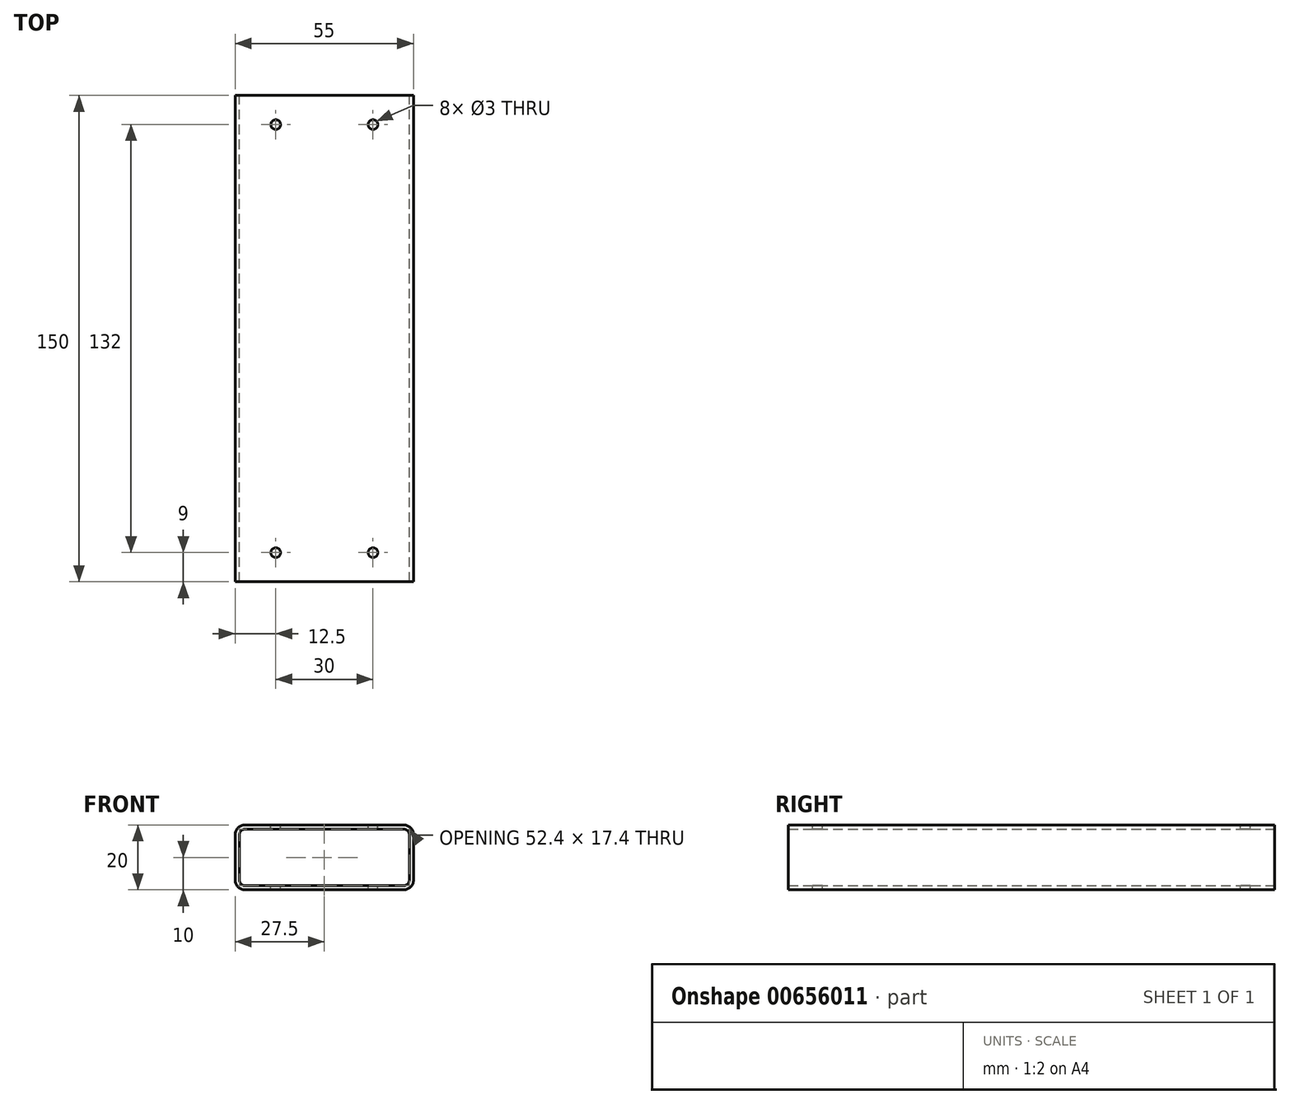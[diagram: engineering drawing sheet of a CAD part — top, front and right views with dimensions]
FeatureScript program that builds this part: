
annotation { "Feature Type Name" : "Feature", "Feature Type Description" : "" }
export const myFeature = defineFeature(function(context is Context, id is Id, definition is map)
    precondition{}
    {
        {
            var Q0;
            Q0=qCreatedBy(makeId("Front.planeOp"),FACE);
            var sketch = newSketch(context, id + "F0", { "sketchPlane" : qUnion([Q0])});
            skLineSegment(sketch, "E0.bottom", {"start": v(-24.5, 10) * mm, "end": v(24.5, 10) * mm});
            skLineSegment(sketch, "E0.top", {"start": v(-24.5, -10) * mm, "end": v(24.5, -10) * mm});
            skLineSegment(sketch, "E0.left", {"start": v(-27.5, 7) * mm, "end": v(-27.5, -7) * mm});
            skLineSegment(sketch, "E0.right", {"start": v(27.5, 7) * mm, "end": v(27.5, -7) * mm});
            skPoint(sketch, "E0.middle", {"position": v(0, 0) * mm});
            skLineSegment(sketch, "E1.bottom", {"start": v(-24.5, 8.7) * mm, "end": v(24.5, 8.7) * mm});
            skLineSegment(sketch, "E1.top", {"start": v(-24.5, -8.7) * mm, "end": v(24.5, -8.7) * mm});
            skLineSegment(sketch, "E1.left", {"start": v(-26.2, 7) * mm, "end": v(-26.2, -7) * mm});
            skLineSegment(sketch, "E1.right", {"start": v(26.2, 7) * mm, "end": v(26.2, -7) * mm});
            skPoint(sketch, "E2.visualSharp", {"position": v(-26.2, 8.7) * mm});
            skArc(sketch, "E2.filletArc", {"start": v(-24.5, 8.7) * mm, "mid": v(-25.7, 8.2) * mm, "end": v(-26.2, 7) * mm});
            skPoint(sketch, "E3.visualSharp", {"position": v(26.2, 8.7) * mm});
            skArc(sketch, "E3.filletArc", {"start": v(26.2, 7) * mm, "mid": v(25.7, 8.2) * mm, "end": v(24.5, 8.7) * mm});
            skPoint(sketch, "E4.visualSharp", {"position": v(26.2, -8.7) * mm});
            skArc(sketch, "E4.filletArc", {"start": v(24.5, -8.7) * mm, "mid": v(25.7, -8.2) * mm, "end": v(26.2, -7) * mm});
            skPoint(sketch, "E5.visualSharp", {"position": v(-26.2, -8.7) * mm});
            skArc(sketch, "E5.filletArc", {"start": v(-26.2, -7) * mm, "mid": v(-25.7, -8.2) * mm, "end": v(-24.5, -8.7) * mm});
            skPoint(sketch, "E6.visualSharp", {"position": v(-27.5, 10) * mm});
            skArc(sketch, "E6.filletArc", {"start": v(-24.5, 10) * mm, "mid": v(-26.62, 9.12) * mm, "end": v(-27.5, 7) * mm});
            skPoint(sketch, "E7.visualSharp", {"position": v(27.5, 10) * mm});
            skArc(sketch, "E7.filletArc", {"start": v(27.5, 7) * mm, "mid": v(26.62, 9.12) * mm, "end": v(24.5, 10) * mm});
            skPoint(sketch, "E8.visualSharp", {"position": v(27.5, -10) * mm});
            skArc(sketch, "E8.filletArc", {"start": v(24.5, -10) * mm, "mid": v(26.62, -9.12) * mm, "end": v(27.5, -7) * mm});
            skPoint(sketch, "E9.visualSharp", {"position": v(-27.5, -10) * mm});
            skArc(sketch, "E9.filletArc", {"start": v(-27.5, -7) * mm, "mid": v(-26.62, -9.12) * mm, "end": v(-24.5, -10) * mm});
            skSolve(sketch);
        }
        {
            var Q0;
            Q0=makeQuery(id+"F0.imprint","IMPRINT",FACE,{"disambiguationData":[TD([[makeQuery(id+"F0.imprint","IMPRINT",EDGE,{"derivedFrom":sQuery(id+"F0.wireOp",EDGE,"E0.bottom")}),-1.0]])]});
            extrude(context, id + "F1", {"entities" : qUnion([Q0]), "depth" : 150 * mm, "offsetDistance" : 25 * mm});
        }
        {
            var Q0;
            Q0=qCreatedBy(makeId("Top.planeOp"),FACE);
            var sketch = newSketch(context, id + "F2", { "sketchPlane" : qUnion([Q0])});
            skCircle(sketch, "E10", {"center": v(-15, -9) * mm, "radius": 1.5 * mm});
            skCircle(sketch, "E11", {"center": v(15, -9) * mm, "radius": 1.5 * mm});
            skCircle(sketch, "E12", {"center": v(-15, -141) * mm, "radius": 1.5 * mm});
            skCircle(sketch, "E13", {"center": v(15, -141) * mm, "radius": 1.5 * mm});
            skSolve(sketch);
        }
        {
            var Q0;
            Q0=makeQuery(id+"F2.imprint","IMPRINT",FACE,{"disambiguationData":[TD([[makeQuery(id+"F2.imprint","IMPRINT",EDGE,{"derivedFrom":sQuery(id+"F2.wireOp",EDGE,"E10")}),1.0]])]});
            extrude(context, id + "F3", {"entities" : qUnion([Q0]), "operationType" : NewBodyOperationType.REMOVE, "endBound" : BoundingType.SYMMETRIC, "oppositeDirection" : true, "depth" : 30 * mm, "offsetDistance" : 25 * mm});
        }
        {
            var Q0;
            Q0=makeQuery(id+"F2.imprint","IMPRINT",FACE,{"disambiguationData":[TD([[makeQuery(id+"F2.imprint","IMPRINT",EDGE,{"derivedFrom":sQuery(id+"F2.wireOp",EDGE,"E11")}),1.0]])]});
            extrude(context, id + "F4", {"entities" : qUnion([Q0]), "operationType" : NewBodyOperationType.REMOVE, "endBound" : BoundingType.SYMMETRIC, "oppositeDirection" : true, "depth" : 30 * mm, "offsetDistance" : 25 * mm});
        }
        {
            var Q0;
            Q0=makeQuery(id+"F2.imprint","IMPRINT",FACE,{"disambiguationData":[TD([[makeQuery(id+"F2.imprint","IMPRINT",EDGE,{"derivedFrom":sQuery(id+"F2.wireOp",EDGE,"E13")}),1.0]])]});
            var Q1;
            Q1=makeQuery(id+"F2.imprint","IMPRINT",FACE,{"disambiguationData":[TD([[makeQuery(id+"F2.imprint","IMPRINT",EDGE,{"derivedFrom":sQuery(id+"F2.wireOp",EDGE,"E12")}),1.0]])]});
            extrude(context, id + "F5", {"entities" : qUnion([Q0, Q1]), "operationType" : NewBodyOperationType.REMOVE, "endBound" : BoundingType.SYMMETRIC, "oppositeDirection" : true, "depth" : 30 * mm, "offsetDistance" : 25 * mm});
        }
    });
